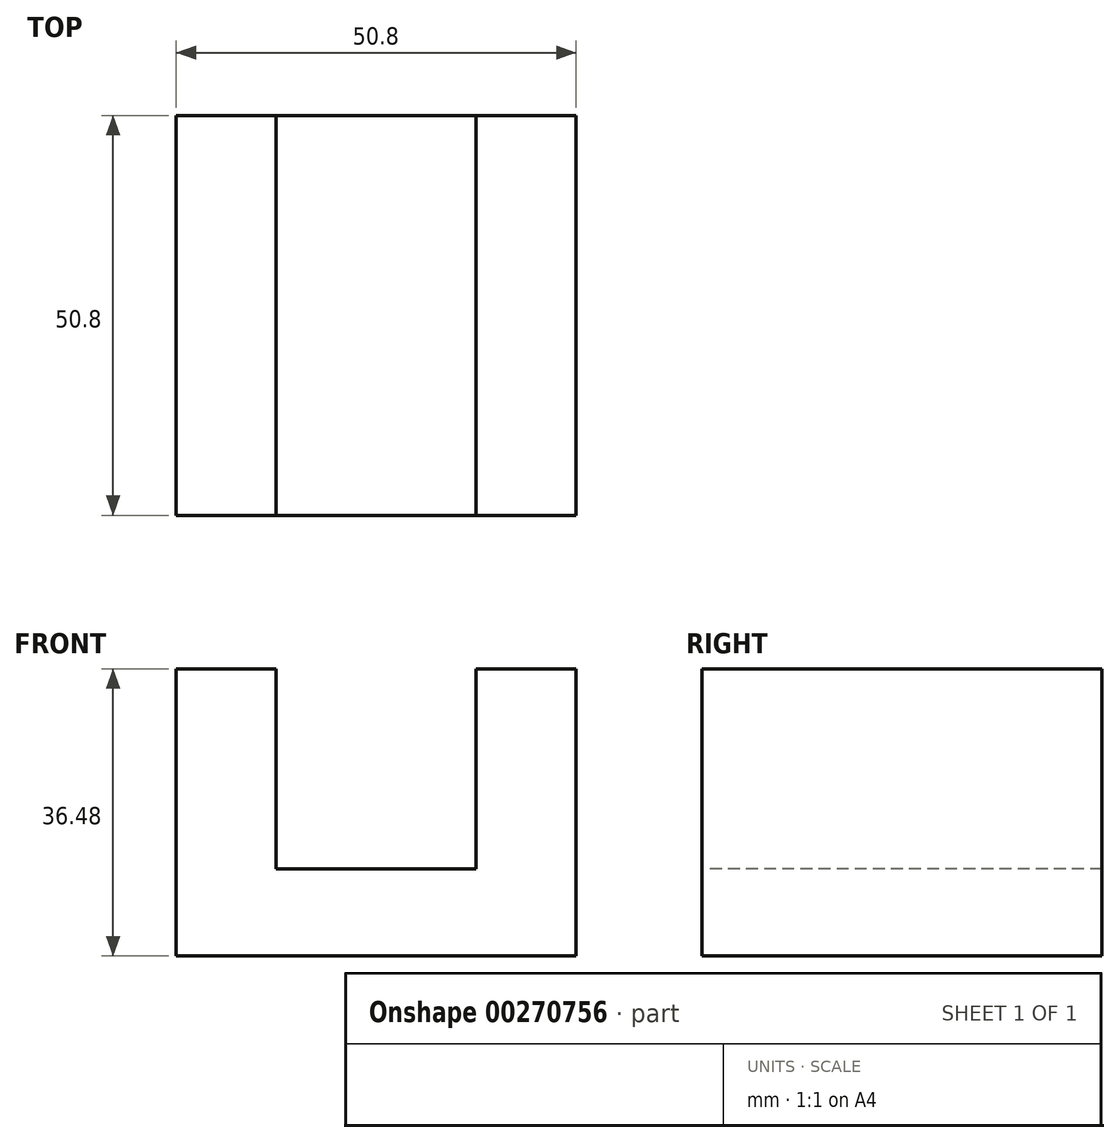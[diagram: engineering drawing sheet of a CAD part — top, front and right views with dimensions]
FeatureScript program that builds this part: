
annotation { "Feature Type Name" : "Feature", "Feature Type Description" : "" }
export const myFeature = defineFeature(function(context is Context, id is Id, definition is map)
    precondition{}
    {
        {
            var Q0;
            Q0=qCreatedBy(makeId("Front.planeOp"),FACE);
            var sketch = newSketch(context, id + "F0", { "sketchPlane" : qUnion([Q0])});
            skLineSegment(sketch, "E0.bottom", {"start": v(0, 0) * mm, "end": v(-50.8, 0) * mm});
            skLineSegment(sketch, "E0.top", {"start": v(0, 50.8) * mm, "end": v(-50.8, 50.8) * mm});
            skLineSegment(sketch, "E0.left", {"start": v(0, 0) * mm, "end": v(0, 50.8) * mm});
            skLineSegment(sketch, "E0.right", {"start": v(-50.8, 0) * mm, "end": v(-50.8, 50.8) * mm});
            skSolve(sketch);
        }
        {
            var Q0;
            Q0 = qSketchRegion(id + "F0", true);
            extrude(context, id + "F1", {"entities" : qUnion([Q0]), "depth" : 50.8 * mm});
        }
        {
            var Q0;
            Q0=makeQuery(id+"F1.opExtrude","CAP_FACE",FACE,{"disambiguationData":[OSD([sQuery(id+"F0.wireOp",EDGE,"E0.bottom"),sQuery(id+"F0.wireOp",EDGE,"E0.top"),sQuery(id+"F0.wireOp",EDGE,"E0.left"),sQuery(id+"F0.wireOp",EDGE,"E0.right")])],"isStart":false});
            var sketch = newSketch(context, id + "F2", { "sketchPlane" : qUnion([Q0])});
            skLineSegment(sketch, "E1", {"start": v(-50.8, 50.8) * mm, "end": v(-38.1, 50.8) * mm});
            skLineSegment(sketch, "E2", {"start": v(-38.1, 50.8) * mm, "end": v(-38.1, 25.4) * mm});
            skLineSegment(sketch, "E3", {"start": v(-38.1, 25.4) * mm, "end": v(-12.7, 25.4) * mm});
            skLineSegment(sketch, "E4", {"start": v(-12.7, 25.4) * mm, "end": v(-12.7, 50.8) * mm});
            skLineSegment(sketch, "E5", {"start": v(-12.7, 50.8) * mm, "end": v(0, 50.8) * mm});
            skLineSegment(sketch, "E6", {"start": v(0, 50.8) * mm, "end": v(0, 14.32) * mm});
            skLineSegment(sketch, "E7", {"start": v(-50.8, 14.32) * mm, "end": v(-50.8, 50.8) * mm});
            skLineSegment(sketch, "E8", {"start": v(-50.8, 14.32) * mm, "end": v(0, 14.32) * mm});
            skSolve(sketch);
        }
        {
            var Q0;
            Q0=makeQuery(id+"F2.imprint","IMPRINT",FACE,{"disambiguationData":[TD([[makeQuery(id+"F2.imprint","IMPRINT",EDGE,{"derivedFrom":sQuery(id+"F2.wireOp",EDGE,"E1")}),1.0]])]});
            extrude(context, id + "F3", {"entities" : qUnion([Q0]), "operationType" : NewBodyOperationType.INTERSECT, "oppositeDirection" : true, "depth" : 50.8 * mm});
        }
    });
